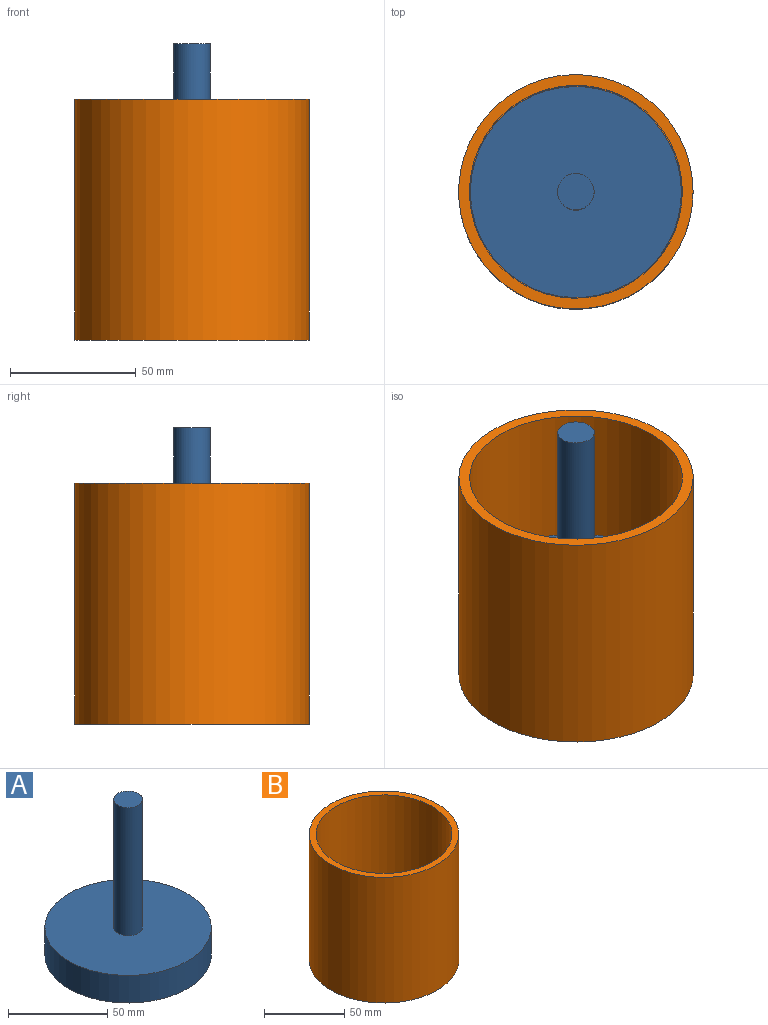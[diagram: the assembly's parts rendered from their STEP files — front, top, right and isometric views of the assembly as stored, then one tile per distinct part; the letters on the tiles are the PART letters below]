
ASSEMBLY  parts=2 mates=1
PART A: 5 faces, bbox 83.8x83.8x96 mm
  f0: cylinder r=41.91mm len=83.82mm, axis (0,0,-1), area 4481.3mm2, adj f1,f2
  f1: plane 83.82x83.82mm, normal (0,0,1), area 5352.9mm2, adj f0,f3
  f2: plane 83.82x83.82mm, normal (0,0,-1), area 5518mm2, adj f0
  f3: cylinder r=7.25mm len=78.99mm, axis (0,0,-1), area 3598.7mm2, adj f1,f4
  f4: plane 14.5x14.5mm, normal (0,0,1), area 165.2mm2, adj f3
PART B: 5 faces, bbox 93.1x93.1x95.8 mm
  f0: cylinder r=46.56mm len=95.76mm, axis (0,0,1), area 28015.6mm2, adj f1,f3
  f1: plane 93.13x93.13mm, normal (0,0,-1), area 6811.4mm2, adj f0
  f2: cylinder r=42.29mm len=87.63mm, axis (0,0,-1), area 23285.2mm2, adj f3,f4
  f3: plane 93.13x93.13mm, normal (0,0,1), area 1192.6mm2, adj f0,f2
  f4: plane 84.58x84.58mm, normal (0,0,1), area 5618.8mm2, adj f2
PLACE A t=(20.97,54.46,-62.68)mm
PLACE B t=(20.97,54.46,-76.25)mm
MATE slider B.f2 <-> A.f0  axis (0,0,-1) through (20.97,54.46,-32.43)mm
